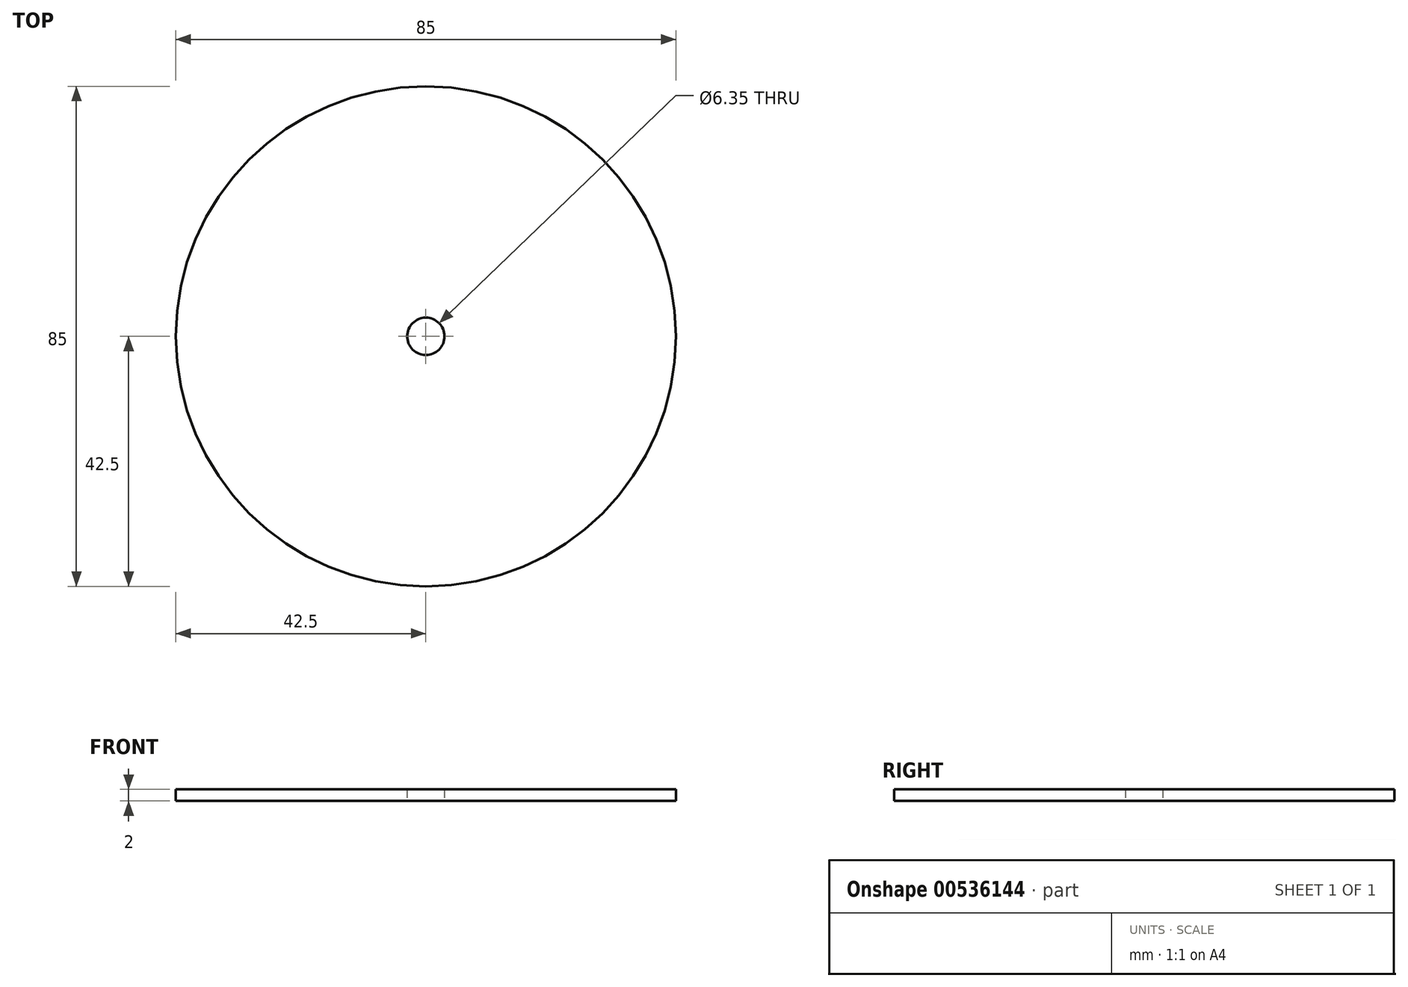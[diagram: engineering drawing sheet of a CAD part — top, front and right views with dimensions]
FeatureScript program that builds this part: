
annotation { "Feature Type Name" : "Feature", "Feature Type Description" : "" }
export const myFeature = defineFeature(function(context is Context, id is Id, definition is map)
    precondition{}
    {
        {
            var Q0;
            Q0=qCreatedBy(makeId("Top.planeOp"),FACE);
            var sketch = newSketch(context, id + "F0", { "sketchPlane" : qUnion([Q0])});
            skCircle(sketch, "E0.0", {"center": v(0, 0) * mm, "radius": 3.18 * mm});
            skCircle(sketch, "E1", {"center": v(0, 0) * mm, "radius": 42.5 * mm});
            skSolve(sketch);
        }
        {
            var Q0;
            Q0=makeQuery(id+"F0.imprint","IMPRINT",FACE,{"disambiguationData":[TD([[makeQuery(id+"F0.imprint","IMPRINT",EDGE,{"derivedFrom":sQuery(id+"F0.wireOp",EDGE,"E0.0")}),-1.0]])]});
            extrude(context, id + "F1", {"entities" : qUnion([Q0]), "depth" : 2 * mm});
        }
    });
